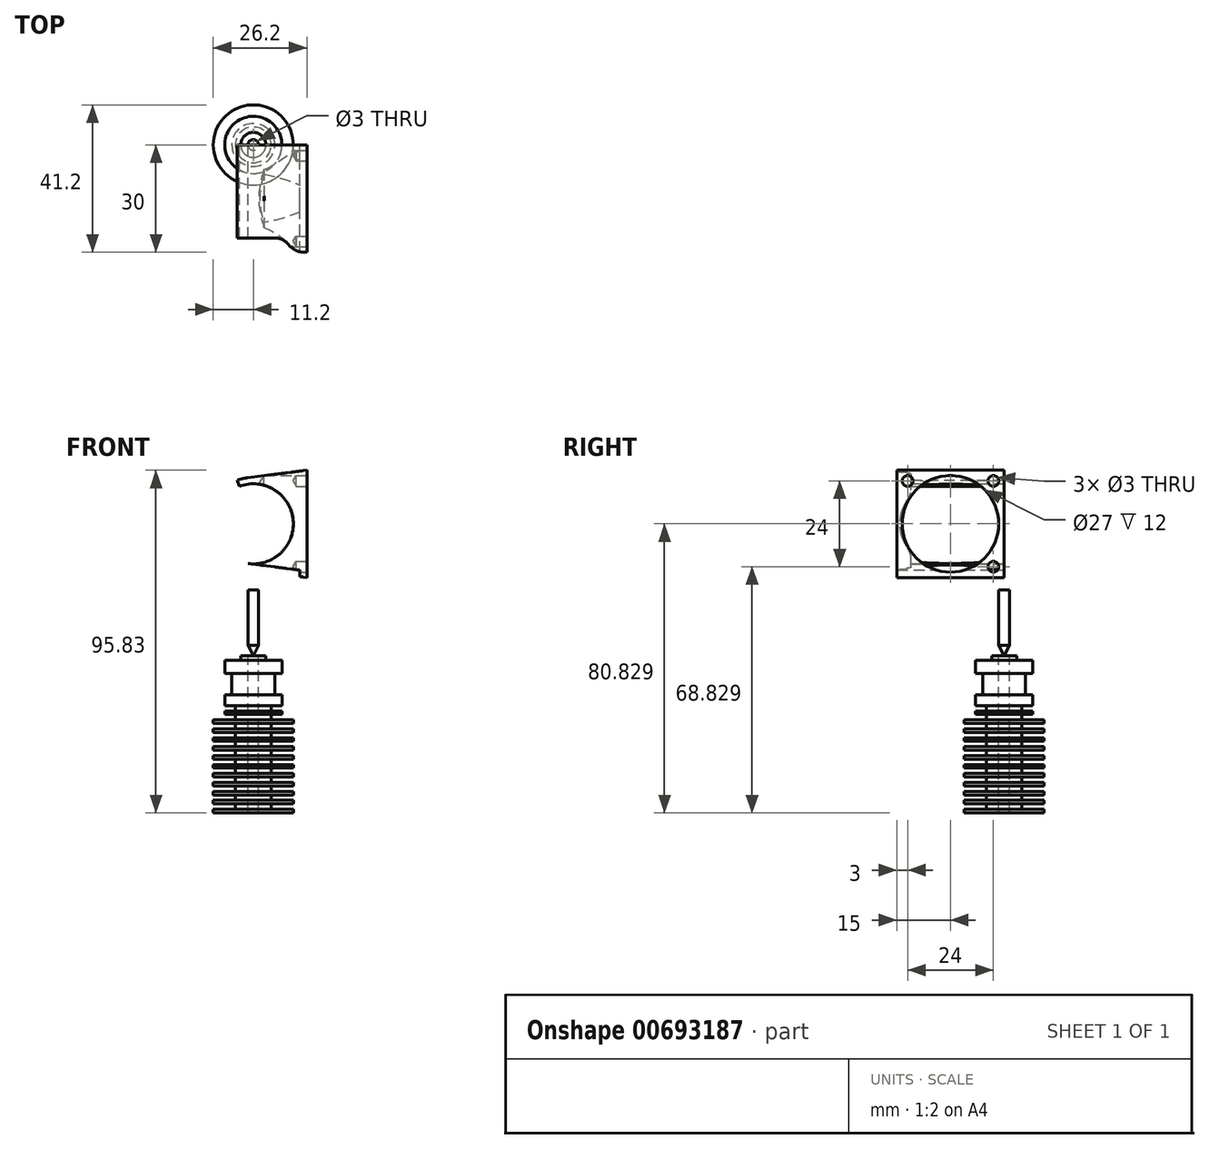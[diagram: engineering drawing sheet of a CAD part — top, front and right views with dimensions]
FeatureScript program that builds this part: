
annotation { "Feature Type Name" : "Feature", "Feature Type Description" : "" }
export const myFeature = defineFeature(function(context is Context, id is Id, definition is map)
    precondition{}
    {
        {
            var Q0;
            Q0=qCreatedBy(makeId("Front.planeOp"),FACE);
            var sketch = newSketch(context, id + "F0", { "sketchPlane" : qUnion([Q0])});
            skLineSegment(sketch, "E0.bottom", {"start": v(-3.5, 0) * mm, "end": v(3.5, 0) * mm});
            skLineSegment(sketch, "E0.top", {"start": v(-3.5, -1.2) * mm, "end": v(3.5, -1.2) * mm});
            skLineSegment(sketch, "E0.left", {"start": v(-3.5, 0) * mm, "end": v(-3.5, -1.2) * mm});
            skLineSegment(sketch, "E0.right", {"start": v(3.5, 0) * mm, "end": v(3.5, -1.2) * mm});
            skPoint(sketch, "E1", {"position": v(0, 0) * mm});
            skLineSegment(sketch, "E2", {"start": v(0, 5.65) * mm, "end": v(0, -51.62) * mm});
            skLineSegment(sketch, "E3.bottom", {"start": v(-8, -1.2) * mm, "end": v(8, -1.2) * mm});
            skLineSegment(sketch, "E3.top", {"start": v(-8, -4.9) * mm, "end": v(8, -4.9) * mm});
            skLineSegment(sketch, "E3.left", {"start": v(-8, -1.2) * mm, "end": v(-8, -4.9) * mm});
            skLineSegment(sketch, "E3.right", {"start": v(8, -1.2) * mm, "end": v(8, -4.9) * mm});
            skLineSegment(sketch, "E4.bottom", {"start": v(-8, -10.9) * mm, "end": v(8, -10.9) * mm});
            skLineSegment(sketch, "E4.top", {"start": v(-8, -13.9) * mm, "end": v(8, -13.9) * mm});
            skLineSegment(sketch, "E4.left", {"start": v(-8, -10.9) * mm, "end": v(-8, -13.9) * mm});
            skLineSegment(sketch, "E4.right", {"start": v(8, -10.9) * mm, "end": v(8, -13.9) * mm});
            skLineSegment(sketch, "E5.bottom", {"start": v(-6, -4.9) * mm, "end": v(6, -4.9) * mm});
            skLineSegment(sketch, "E5.top", {"start": v(-6, -10.9) * mm, "end": v(6, -10.9) * mm});
            skLineSegment(sketch, "E5.left", {"start": v(-6, -4.9) * mm, "end": v(-6, -10.9) * mm});
            skLineSegment(sketch, "E5.right", {"start": v(6, -4.9) * mm, "end": v(6, -10.9) * mm});
            skLineSegment(sketch, "E6.bottom", {"start": v(-11.2, -17.9) * mm, "end": v(11.2, -17.9) * mm});
            skLineSegment(sketch, "E6.top", {"start": v(-11.2, -18.9) * mm, "end": v(11.2, -18.9) * mm});
            skLineSegment(sketch, "E6.left", {"start": v(-11.2, -17.9) * mm, "end": v(-11.2, -18.9) * mm});
            skLineSegment(sketch, "E6.right", {"start": v(11.2, -17.9) * mm, "end": v(11.2, -18.9) * mm});
            skLineSegment(sketch, "E7.bottom", {"start": v(-8, -15.4) * mm, "end": v(8, -15.4) * mm});
            skLineSegment(sketch, "E7.top", {"start": v(-8, -16.4) * mm, "end": v(8, -16.4) * mm});
            skLineSegment(sketch, "E7.left", {"start": v(-8, -15.4) * mm, "end": v(-8, -16.4) * mm});
            skLineSegment(sketch, "E7.right", {"start": v(8, -15.4) * mm, "end": v(8, -16.4) * mm});
            skLineSegment(sketch, "E8.bottom", {"start": v(-5, -16.4) * mm, "end": v(5, -16.4) * mm});
            skLineSegment(sketch, "E8.top", {"start": v(-5, -43.9) * mm, "end": v(5, -43.9) * mm});
            skLineSegment(sketch, "E8.left", {"start": v(-5, -16.4) * mm, "end": v(-5, -43.9) * mm});
            skLineSegment(sketch, "E8.right", {"start": v(5, -16.4) * mm, "end": v(5, -43.9) * mm});
            skLineSegment(sketch, "E9.bottom", {"start": v(-5, -13.9) * mm, "end": v(5, -13.9) * mm});
            skLineSegment(sketch, "E9.top", {"start": v(-5, -15.4) * mm, "end": v(5, -15.4) * mm});
            skLineSegment(sketch, "E9.left", {"start": v(-5, -13.9) * mm, "end": v(-5, -15.4) * mm});
            skLineSegment(sketch, "E9.right", {"start": v(5, -13.9) * mm, "end": v(5, -15.4) * mm});
            skLineSegment(sketch, "E10", {"start": v(-23.04, -43.9) * mm, "end": v(22.42, -43.9) * mm, "construction": true});
            skLineSegment(sketch, "E11.bottom", {"start": v(-11.2, -42.9) * mm, "end": v(11.2, -42.9) * mm});
            skLineSegment(sketch, "E11.top", {"start": v(-11.2, -43.9) * mm, "end": v(11.2, -43.9) * mm});
            skLineSegment(sketch, "E11.left", {"start": v(-11.2, -42.9) * mm, "end": v(-11.2, -43.9) * mm});
            skLineSegment(sketch, "E11.right", {"start": v(11.2, -42.9) * mm, "end": v(11.2, -43.9) * mm});
            skLineSegment(sketch, "E12.bottom", {"start": v(-11.2, -40.4) * mm, "end": v(11.2, -40.4) * mm});
            skLineSegment(sketch, "E12.top", {"start": v(-11.2, -41.4) * mm, "end": v(11.2, -41.4) * mm});
            skLineSegment(sketch, "E12.left", {"start": v(-11.2, -40.4) * mm, "end": v(-11.2, -41.4) * mm});
            skLineSegment(sketch, "E12.right", {"start": v(11.2, -40.4) * mm, "end": v(11.2, -41.4) * mm});
            skLineSegment(sketch, "E13.bottom", {"start": v(-11.2, -37.9) * mm, "end": v(11.2, -37.9) * mm});
            skLineSegment(sketch, "E13.top", {"start": v(-11.2, -38.9) * mm, "end": v(11.2, -38.9) * mm});
            skLineSegment(sketch, "E13.left", {"start": v(-11.2, -37.9) * mm, "end": v(-11.2, -38.9) * mm});
            skLineSegment(sketch, "E13.right", {"start": v(11.2, -37.9) * mm, "end": v(11.2, -38.9) * mm});
            skLineSegment(sketch, "E14.bottom", {"start": v(-11.2, -35.4) * mm, "end": v(11.2, -35.4) * mm});
            skLineSegment(sketch, "E14.top", {"start": v(-11.2, -36.4) * mm, "end": v(11.2, -36.4) * mm});
            skLineSegment(sketch, "E14.left", {"start": v(-11.2, -35.4) * mm, "end": v(-11.2, -36.4) * mm});
            skLineSegment(sketch, "E14.right", {"start": v(11.2, -35.4) * mm, "end": v(11.2, -36.4) * mm});
            skLineSegment(sketch, "E15.bottom", {"start": v(-11.2, -32.9) * mm, "end": v(11.2, -32.9) * mm});
            skLineSegment(sketch, "E15.top", {"start": v(-11.2, -33.9) * mm, "end": v(11.2, -33.9) * mm});
            skLineSegment(sketch, "E15.left", {"start": v(-11.2, -32.9) * mm, "end": v(-11.2, -33.9) * mm});
            skLineSegment(sketch, "E15.right", {"start": v(11.2, -32.9) * mm, "end": v(11.2, -33.9) * mm});
            skLineSegment(sketch, "E16.bottom", {"start": v(-11.2, -30.4) * mm, "end": v(11.2, -30.4) * mm});
            skLineSegment(sketch, "E16.top", {"start": v(-11.2, -31.4) * mm, "end": v(11.2, -31.4) * mm});
            skLineSegment(sketch, "E16.left", {"start": v(-11.2, -30.4) * mm, "end": v(-11.2, -31.4) * mm});
            skLineSegment(sketch, "E16.right", {"start": v(11.2, -30.4) * mm, "end": v(11.2, -31.4) * mm});
            skLineSegment(sketch, "E17.bottom", {"start": v(-11.2, -27.9) * mm, "end": v(11.2, -27.9) * mm});
            skLineSegment(sketch, "E17.top", {"start": v(-11.2, -28.9) * mm, "end": v(11.2, -28.9) * mm});
            skLineSegment(sketch, "E17.left", {"start": v(-11.2, -27.9) * mm, "end": v(-11.2, -28.9) * mm});
            skLineSegment(sketch, "E17.right", {"start": v(11.2, -27.9) * mm, "end": v(11.2, -28.9) * mm});
            skLineSegment(sketch, "E18.bottom", {"start": v(-11.2, -25.4) * mm, "end": v(11.2, -25.4) * mm});
            skLineSegment(sketch, "E18.top", {"start": v(-11.2, -26.4) * mm, "end": v(11.2, -26.4) * mm});
            skLineSegment(sketch, "E18.left", {"start": v(-11.2, -25.4) * mm, "end": v(-11.2, -26.4) * mm});
            skLineSegment(sketch, "E18.right", {"start": v(11.2, -25.4) * mm, "end": v(11.2, -26.4) * mm});
            skLineSegment(sketch, "E19.bottom", {"start": v(-11.2, -22.9) * mm, "end": v(11.2, -22.9) * mm});
            skLineSegment(sketch, "E19.top", {"start": v(-11.2, -23.9) * mm, "end": v(11.2, -23.9) * mm});
            skLineSegment(sketch, "E19.left", {"start": v(-11.2, -22.9) * mm, "end": v(-11.2, -23.9) * mm});
            skLineSegment(sketch, "E19.right", {"start": v(11.2, -22.9) * mm, "end": v(11.2, -23.9) * mm});
            skLineSegment(sketch, "E20.bottom", {"start": v(-11.2, -20.4) * mm, "end": v(11.2, -20.4) * mm});
            skLineSegment(sketch, "E20.top", {"start": v(-11.2, -21.4) * mm, "end": v(11.2, -21.4) * mm});
            skLineSegment(sketch, "E20.left", {"start": v(-11.2, -20.4) * mm, "end": v(-11.2, -21.4) * mm});
            skLineSegment(sketch, "E20.right", {"start": v(11.2, -20.4) * mm, "end": v(11.2, -21.4) * mm});
            skLineSegment(sketch, "E21.bottom", {"start": v(29.22, -43.9) * mm, "end": v(59.22, -43.9) * mm});
            skLineSegment(sketch, "E21.top", {"start": v(29.22, -13.9) * mm, "end": v(59.22, -13.9) * mm});
            skLineSegment(sketch, "E21.left", {"start": v(29.22, -43.9) * mm, "end": v(29.22, -13.9) * mm});
            skLineSegment(sketch, "E21.right", {"start": v(59.22, -43.9) * mm, "end": v(59.22, -13.9) * mm});
            skLineSegment(sketch, "E22", {"start": v(87.52, -43.9) * mm, "end": v(112.52, -43.9) * mm});
            skLineSegment(sketch, "E23", {"start": v(112.52, -43.9) * mm, "end": v(112.52, -13.9) * mm});
            skLineSegment(sketch, "E24", {"start": v(112.52, -13.9) * mm, "end": v(102.52, -13.9) * mm});
            skLineSegment(sketch, "E25", {"start": v(102.52, -13.9) * mm, "end": v(102.52, -17.9) * mm});
            skLineSegment(sketch, "E26", {"start": v(102.52, -17.9) * mm, "end": v(87.52, -17.9) * mm});
            skLineSegment(sketch, "E27", {"start": v(87.52, -17.9) * mm, "end": v(87.52, -43.9) * mm});
            skCircle(sketch, "E28", {"center": v(0, 36.93) * mm, "radius": 11.2 * mm, "construction": true});
            skCircle(sketch, "E29", {"center": v(0, 36.93) * mm, "radius": 13 * mm, "construction": true});
            skLineSegment(sketch, "E30.right", {"start": v(25, 21.93) * mm, "end": v(25, 51.93) * mm});
            skLineSegment(sketch, "E31.right", {"start": v(15, 21.93) * mm, "end": v(15, 51.93) * mm});
            skLineSegment(sketch, "E32", {"start": v(15, 51.93) * mm, "end": v(-1.63, 49.83) * mm});
            skLineSegment(sketch, "E33", {"start": v(15, 21.93) * mm, "end": v(-1.63, 24.03) * mm});
            skLineSegment(sketch, "E34", {"start": v(15, 21.93) * mm, "end": v(25, 21.93) * mm});
            skLineSegment(sketch, "E35", {"start": v(15, 51.93) * mm, "end": v(25, 51.93) * mm});
            skLineSegment(sketch, "E36", {"start": v(0, 36.93) * mm, "end": v(-4.45, 49.15) * mm});
            skArc(sketch, "E37", {"start": v(-1.63, 49.83) * mm, "mid": v(-3.06, 49.56) * mm, "end": v(-4.45, 49.15) * mm});
            skPoint(sketch, "E38", {"position": v(15, 50.13) * mm});
            skPoint(sketch, "E39", {"position": v(15, 23.73) * mm});
            skLineSegment(sketch, "E40", {"start": v(15, 23.73) * mm, "end": v(-1.41, 25.82) * mm});
            skLineSegment(sketch, "E41", {"start": v(15, 50.13) * mm, "end": v(-1.41, 48.04) * mm});
            skLineSegment(sketch, "E42", {"start": v(0, 36.93) * mm, "end": v(-4.45, 24.71) * mm});
            skArc(sketch, "E43", {"start": v(-3.83, 47.45) * mm, "mid": v(11.2, 36.93) * mm, "end": v(-3.83, 26.4) * mm});
            skArc(sketch, "E44", {"start": v(-1.63, 24.03) * mm, "mid": v(-3.06, 24.3) * mm, "end": v(-4.45, 24.71) * mm});
            skLineSegment(sketch, "E45", {"start": v(0, 36.93) * mm, "end": v(33.8, 36.93) * mm, "construction": true});
            skLineSegment(sketch, "E46", {"start": v(13, 51.68) * mm, "end": v(13, 22.18) * mm});
            skSolve(sketch);
        }
        {
            var Q0;
            {var subQ0=sQuery(id+"F0.wireOp",EDGE,"E3.left");Q0=makeQuery(id+"F0.imprint","IMPRINT",FACE,{"disambiguationData":[TD([[makeQuery(id+"F0.imprint","IMPRINT",EDGE,{"derivedFrom":subQ0}),1.0]])]});}
            var Q1;
            {var subQ0=sQuery(id+"F0.wireOp",EDGE,"E0.left");Q1=makeQuery(id+"F0.imprint","IMPRINT",FACE,{"disambiguationData":[TD([[makeQuery(id+"F0.imprint","IMPRINT",EDGE,{"derivedFrom":subQ0}),1.0]])]});}
            var Q2;
            {var subQ5=sQuery(id+"F0.wireOp",EDGE,"E5.left");Q2=makeQuery(id+"F0.imprint","IMPRINT",FACE,{"disambiguationData":[TD([[makeQuery(id+"F0.imprint","IMPRINT",EDGE,{"derivedFrom":subQ5}),1.0]])]});}
            var Q3;
            {var subQ0=sQuery(id+"F0.wireOp",EDGE,"E4.left");Q3=makeQuery(id+"F0.imprint","IMPRINT",FACE,{"disambiguationData":[TD([[makeQuery(id+"F0.imprint","IMPRINT",EDGE,{"derivedFrom":subQ0}),1.0]])]});}
            var Q4;
            {var subQ5=sQuery(id+"F0.wireOp",EDGE,"E9.left");Q4=makeQuery(id+"F0.imprint","IMPRINT",FACE,{"disambiguationData":[TD([[makeQuery(id+"F0.imprint","IMPRINT",EDGE,{"derivedFrom":subQ5}),1.0]])]});}
            var Q5;
            {var subQ0=sQuery(id+"F0.wireOp",EDGE,"E7.left");Q5=makeQuery(id+"F0.imprint","IMPRINT",FACE,{"disambiguationData":[TD([[makeQuery(id+"F0.imprint","IMPRINT",EDGE,{"derivedFrom":subQ0}),1.0]])]});}
            var Q6;
            {var subQ0=sQuery(id+"F0.wireOp",EDGE,"E8.bottom");var subQ1=sQuery(id+"F0.wireOp",EDGE,"E2");var subQ2=makeQuery(id+"F0.imprint","INTERSECT",VERTEX,{"derivedFrom":[subQ1,subQ0]});Q6=makeQuery(id+"F0.imprint","IMPRINT",FACE,{"disambiguationData":[TD([[makeQuery(id+"F0.imprint","IMPRINT",EDGE,{"disambiguationData":[TD([[subQ2,-1.0]])],"derivedFrom":subQ1}),-1.0]])]});}
            var Q7;
            {var subQ0=sQuery(id+"F0.wireOp",EDGE,"E6.bottom");var subQ1=sQuery(id+"F0.wireOp",EDGE,"E2");var subQ2=makeQuery(id+"F0.imprint","INTERSECT",VERTEX,{"derivedFrom":[subQ1,subQ0]});Q7=makeQuery(id+"F0.imprint","IMPRINT",FACE,{"disambiguationData":[TD([[makeQuery(id+"F0.imprint","IMPRINT",EDGE,{"disambiguationData":[TD([[subQ2,-1.0]])],"derivedFrom":subQ1}),-1.0]])]});}
            var Q8;
            {var subQ0=sQuery(id+"F0.wireOp",EDGE,"E6.top");var subQ1=sQuery(id+"F0.wireOp",EDGE,"E2");var subQ2=makeQuery(id+"F0.imprint","INTERSECT",VERTEX,{"derivedFrom":[subQ1,subQ0]});Q8=makeQuery(id+"F0.imprint","IMPRINT",FACE,{"disambiguationData":[TD([[makeQuery(id+"F0.imprint","IMPRINT",EDGE,{"disambiguationData":[TD([[subQ2,-1.0]])],"derivedFrom":subQ1}),-1.0]])]});}
            var Q9;
            {var subQ0=sQuery(id+"F0.wireOp",EDGE,"E20.bottom");var subQ1=sQuery(id+"F0.wireOp",EDGE,"E2");var subQ2=makeQuery(id+"F0.imprint","INTERSECT",VERTEX,{"derivedFrom":[subQ1,subQ0]});Q9=makeQuery(id+"F0.imprint","IMPRINT",FACE,{"disambiguationData":[TD([[makeQuery(id+"F0.imprint","IMPRINT",EDGE,{"disambiguationData":[TD([[subQ2,-1.0]])],"derivedFrom":subQ1}),-1.0]])]});}
            var Q10;
            {var subQ0=sQuery(id+"F0.wireOp",EDGE,"E19.bottom");var subQ1=sQuery(id+"F0.wireOp",EDGE,"E2");var subQ2=makeQuery(id+"F0.imprint","INTERSECT",VERTEX,{"derivedFrom":[subQ1,subQ0]});Q10=makeQuery(id+"F0.imprint","IMPRINT",FACE,{"disambiguationData":[TD([[makeQuery(id+"F0.imprint","IMPRINT",EDGE,{"disambiguationData":[TD([[subQ2,-1.0]])],"derivedFrom":subQ1}),-1.0]])]});}
            var Q11;
            {var subQ5=sQuery(id+"F0.wireOp",EDGE,"E20.left");Q11=makeQuery(id+"F0.imprint","IMPRINT",FACE,{"disambiguationData":[TD([[makeQuery(id+"F0.imprint","IMPRINT",EDGE,{"derivedFrom":subQ5}),1.0]])]});}
            var Q12;
            {var subQ5=sQuery(id+"F0.wireOp",EDGE,"E19.left");Q12=makeQuery(id+"F0.imprint","IMPRINT",FACE,{"disambiguationData":[TD([[makeQuery(id+"F0.imprint","IMPRINT",EDGE,{"derivedFrom":subQ5}),1.0]])]});}
            var Q13;
            {var subQ5=sQuery(id+"F0.wireOp",EDGE,"E18.left");Q13=makeQuery(id+"F0.imprint","IMPRINT",FACE,{"disambiguationData":[TD([[makeQuery(id+"F0.imprint","IMPRINT",EDGE,{"derivedFrom":subQ5}),1.0]])]});}
            var Q14;
            {var subQ5=sQuery(id+"F0.wireOp",EDGE,"E17.left");Q14=makeQuery(id+"F0.imprint","IMPRINT",FACE,{"disambiguationData":[TD([[makeQuery(id+"F0.imprint","IMPRINT",EDGE,{"derivedFrom":subQ5}),1.0]])]});}
            var Q15;
            {var subQ5=sQuery(id+"F0.wireOp",EDGE,"E15.left");Q15=makeQuery(id+"F0.imprint","IMPRINT",FACE,{"disambiguationData":[TD([[makeQuery(id+"F0.imprint","IMPRINT",EDGE,{"derivedFrom":subQ5}),1.0]])]});}
            var Q16;
            {var subQ5=sQuery(id+"F0.wireOp",EDGE,"E16.left");Q16=makeQuery(id+"F0.imprint","IMPRINT",FACE,{"disambiguationData":[TD([[makeQuery(id+"F0.imprint","IMPRINT",EDGE,{"derivedFrom":subQ5}),1.0]])]});}
            var Q17;
            {var subQ5=sQuery(id+"F0.wireOp",EDGE,"E13.left");Q17=makeQuery(id+"F0.imprint","IMPRINT",FACE,{"disambiguationData":[TD([[makeQuery(id+"F0.imprint","IMPRINT",EDGE,{"derivedFrom":subQ5}),1.0]])]});}
            var Q18;
            {var subQ5=sQuery(id+"F0.wireOp",EDGE,"E12.left");Q18=makeQuery(id+"F0.imprint","IMPRINT",FACE,{"disambiguationData":[TD([[makeQuery(id+"F0.imprint","IMPRINT",EDGE,{"derivedFrom":subQ5}),1.0]])]});}
            var Q19;
            {var subQ5=sQuery(id+"F0.wireOp",EDGE,"E14.left");Q19=makeQuery(id+"F0.imprint","IMPRINT",FACE,{"disambiguationData":[TD([[makeQuery(id+"F0.imprint","IMPRINT",EDGE,{"derivedFrom":subQ5}),1.0]])]});}
            var Q20;
            {var subQ5=sQuery(id+"F0.wireOp",EDGE,"E11.left");Q20=makeQuery(id+"F0.imprint","IMPRINT",FACE,{"disambiguationData":[TD([[makeQuery(id+"F0.imprint","IMPRINT",EDGE,{"derivedFrom":subQ5}),1.0]])]});}
            var Q21;
            {var subQ0=sQuery(id+"F0.wireOp",EDGE,"E18.bottom");var subQ1=sQuery(id+"F0.wireOp",EDGE,"E2");var subQ2=makeQuery(id+"F0.imprint","INTERSECT",VERTEX,{"derivedFrom":[subQ1,subQ0]});Q21=makeQuery(id+"F0.imprint","IMPRINT",FACE,{"disambiguationData":[TD([[makeQuery(id+"F0.imprint","IMPRINT",EDGE,{"disambiguationData":[TD([[subQ2,-1.0]])],"derivedFrom":subQ1}),-1.0]])]});}
            var Q22;
            {var subQ0=sQuery(id+"F0.wireOp",EDGE,"E6.left");Q22=makeQuery(id+"F0.imprint","IMPRINT",FACE,{"disambiguationData":[TD([[makeQuery(id+"F0.imprint","IMPRINT",EDGE,{"derivedFrom":subQ0}),1.0]])]});}
            var Q23;
            {var subQ0=sQuery(id+"F0.wireOp",EDGE,"E18.top");var subQ1=sQuery(id+"F0.wireOp",EDGE,"E2");var subQ2=makeQuery(id+"F0.imprint","INTERSECT",VERTEX,{"derivedFrom":[subQ1,subQ0]});Q23=makeQuery(id+"F0.imprint","IMPRINT",FACE,{"disambiguationData":[TD([[makeQuery(id+"F0.imprint","IMPRINT",EDGE,{"disambiguationData":[TD([[subQ2,-1.0]])],"derivedFrom":subQ1}),-1.0]])]});}
            var Q24;
            {var subQ0=sQuery(id+"F0.wireOp",EDGE,"E19.top");var subQ1=sQuery(id+"F0.wireOp",EDGE,"E2");var subQ2=makeQuery(id+"F0.imprint","INTERSECT",VERTEX,{"derivedFrom":[subQ1,subQ0]});Q24=makeQuery(id+"F0.imprint","IMPRINT",FACE,{"disambiguationData":[TD([[makeQuery(id+"F0.imprint","IMPRINT",EDGE,{"disambiguationData":[TD([[subQ2,-1.0]])],"derivedFrom":subQ1}),-1.0]])]});}
            var Q25;
            {var subQ0=sQuery(id+"F0.wireOp",EDGE,"E20.top");var subQ1=sQuery(id+"F0.wireOp",EDGE,"E2");var subQ2=makeQuery(id+"F0.imprint","INTERSECT",VERTEX,{"derivedFrom":[subQ1,subQ0]});Q25=makeQuery(id+"F0.imprint","IMPRINT",FACE,{"disambiguationData":[TD([[makeQuery(id+"F0.imprint","IMPRINT",EDGE,{"disambiguationData":[TD([[subQ2,-1.0]])],"derivedFrom":subQ1}),-1.0]])]});}
            var Q26;
            {var subQ0=sQuery(id+"F0.wireOp",EDGE,"E12.top");var subQ1=sQuery(id+"F0.wireOp",EDGE,"E2");var subQ2=makeQuery(id+"F0.imprint","INTERSECT",VERTEX,{"derivedFrom":[subQ1,subQ0]});Q26=makeQuery(id+"F0.imprint","IMPRINT",FACE,{"disambiguationData":[TD([[makeQuery(id+"F0.imprint","IMPRINT",EDGE,{"disambiguationData":[TD([[subQ2,-1.0]])],"derivedFrom":subQ1}),-1.0]])]});}
            var Q27;
            {var subQ0=sQuery(id+"F0.wireOp",EDGE,"E13.top");var subQ1=sQuery(id+"F0.wireOp",EDGE,"E2");var subQ2=makeQuery(id+"F0.imprint","INTERSECT",VERTEX,{"derivedFrom":[subQ1,subQ0]});Q27=makeQuery(id+"F0.imprint","IMPRINT",FACE,{"disambiguationData":[TD([[makeQuery(id+"F0.imprint","IMPRINT",EDGE,{"disambiguationData":[TD([[subQ2,-1.0]])],"derivedFrom":subQ1}),-1.0]])]});}
            var Q28;
            {var subQ0=sQuery(id+"F0.wireOp",EDGE,"E17.top");var subQ1=sQuery(id+"F0.wireOp",EDGE,"E2");var subQ2=makeQuery(id+"F0.imprint","INTERSECT",VERTEX,{"derivedFrom":[subQ1,subQ0]});Q28=makeQuery(id+"F0.imprint","IMPRINT",FACE,{"disambiguationData":[TD([[makeQuery(id+"F0.imprint","IMPRINT",EDGE,{"disambiguationData":[TD([[subQ2,-1.0]])],"derivedFrom":subQ1}),-1.0]])]});}
            var Q29;
            {var subQ0=sQuery(id+"F0.wireOp",EDGE,"E16.top");var subQ1=sQuery(id+"F0.wireOp",EDGE,"E2");var subQ2=makeQuery(id+"F0.imprint","INTERSECT",VERTEX,{"derivedFrom":[subQ1,subQ0]});Q29=makeQuery(id+"F0.imprint","IMPRINT",FACE,{"disambiguationData":[TD([[makeQuery(id+"F0.imprint","IMPRINT",EDGE,{"disambiguationData":[TD([[subQ2,-1.0]])],"derivedFrom":subQ1}),-1.0]])]});}
            var Q30;
            {var subQ0=sQuery(id+"F0.wireOp",EDGE,"E14.top");var subQ1=sQuery(id+"F0.wireOp",EDGE,"E2");var subQ2=makeQuery(id+"F0.imprint","INTERSECT",VERTEX,{"derivedFrom":[subQ1,subQ0]});Q30=makeQuery(id+"F0.imprint","IMPRINT",FACE,{"disambiguationData":[TD([[makeQuery(id+"F0.imprint","IMPRINT",EDGE,{"disambiguationData":[TD([[subQ2,-1.0]])],"derivedFrom":subQ1}),-1.0]])]});}
            var Q31;
            {var subQ0=sQuery(id+"F0.wireOp",EDGE,"E17.bottom");var subQ1=sQuery(id+"F0.wireOp",EDGE,"E2");var subQ2=makeQuery(id+"F0.imprint","INTERSECT",VERTEX,{"derivedFrom":[subQ1,subQ0]});Q31=makeQuery(id+"F0.imprint","IMPRINT",FACE,{"disambiguationData":[TD([[makeQuery(id+"F0.imprint","IMPRINT",EDGE,{"disambiguationData":[TD([[subQ2,-1.0]])],"derivedFrom":subQ1}),-1.0]])]});}
            var Q32;
            {var subQ0=sQuery(id+"F0.wireOp",EDGE,"E16.bottom");var subQ1=sQuery(id+"F0.wireOp",EDGE,"E2");var subQ2=makeQuery(id+"F0.imprint","INTERSECT",VERTEX,{"derivedFrom":[subQ1,subQ0]});Q32=makeQuery(id+"F0.imprint","IMPRINT",FACE,{"disambiguationData":[TD([[makeQuery(id+"F0.imprint","IMPRINT",EDGE,{"disambiguationData":[TD([[subQ2,-1.0]])],"derivedFrom":subQ1}),-1.0]])]});}
            var Q33;
            {var subQ0=sQuery(id+"F0.wireOp",EDGE,"E15.bottom");var subQ1=sQuery(id+"F0.wireOp",EDGE,"E2");var subQ2=makeQuery(id+"F0.imprint","INTERSECT",VERTEX,{"derivedFrom":[subQ1,subQ0]});Q33=makeQuery(id+"F0.imprint","IMPRINT",FACE,{"disambiguationData":[TD([[makeQuery(id+"F0.imprint","IMPRINT",EDGE,{"disambiguationData":[TD([[subQ2,-1.0]])],"derivedFrom":subQ1}),-1.0]])]});}
            var Q34;
            {var subQ0=sQuery(id+"F0.wireOp",EDGE,"E12.bottom");var subQ1=sQuery(id+"F0.wireOp",EDGE,"E2");var subQ2=makeQuery(id+"F0.imprint","INTERSECT",VERTEX,{"derivedFrom":[subQ1,subQ0]});Q34=makeQuery(id+"F0.imprint","IMPRINT",FACE,{"disambiguationData":[TD([[makeQuery(id+"F0.imprint","IMPRINT",EDGE,{"disambiguationData":[TD([[subQ2,-1.0]])],"derivedFrom":subQ1}),-1.0]])]});}
            var Q35;
            {var subQ0=sQuery(id+"F0.wireOp",EDGE,"E13.bottom");var subQ1=sQuery(id+"F0.wireOp",EDGE,"E2");var subQ2=makeQuery(id+"F0.imprint","INTERSECT",VERTEX,{"derivedFrom":[subQ1,subQ0]});Q35=makeQuery(id+"F0.imprint","IMPRINT",FACE,{"disambiguationData":[TD([[makeQuery(id+"F0.imprint","IMPRINT",EDGE,{"disambiguationData":[TD([[subQ2,-1.0]])],"derivedFrom":subQ1}),-1.0]])]});}
            var Q36;
            {var subQ0=sQuery(id+"F0.wireOp",EDGE,"E15.top");var subQ1=sQuery(id+"F0.wireOp",EDGE,"E2");var subQ2=makeQuery(id+"F0.imprint","INTERSECT",VERTEX,{"derivedFrom":[subQ1,subQ0]});Q36=makeQuery(id+"F0.imprint","IMPRINT",FACE,{"disambiguationData":[TD([[makeQuery(id+"F0.imprint","IMPRINT",EDGE,{"disambiguationData":[TD([[subQ2,-1.0]])],"derivedFrom":subQ1}),-1.0]])]});}
            var Q37;
            {var subQ0=sQuery(id+"F0.wireOp",EDGE,"E14.bottom");var subQ1=sQuery(id+"F0.wireOp",EDGE,"E2");var subQ2=makeQuery(id+"F0.imprint","INTERSECT",VERTEX,{"derivedFrom":[subQ1,subQ0]});Q37=makeQuery(id+"F0.imprint","IMPRINT",FACE,{"disambiguationData":[TD([[makeQuery(id+"F0.imprint","IMPRINT",EDGE,{"disambiguationData":[TD([[subQ2,-1.0]])],"derivedFrom":subQ1}),-1.0]])]});}
            var Q38;
            {var subQ0=sQuery(id+"F0.wireOp",EDGE,"E11.top");var subQ1=sQuery(id+"F0.wireOp",EDGE,"E2");var subQ2=makeQuery(id+"F0.imprint","INTERSECT",VERTEX,{"derivedFrom":[subQ1,subQ0]});Q38=makeQuery(id+"F0.imprint","IMPRINT",FACE,{"disambiguationData":[TD([[makeQuery(id+"F0.imprint","IMPRINT",EDGE,{"disambiguationData":[TD([[subQ2,1.0]])],"derivedFrom":subQ1}),-1.0]])]});}
            var Q39;
            Q39=sQuery(id+"F0.wireOp",EDGE,"E2");
            revolve(context, id + "F1", {"entities" : qUnion([Q0, Q1, Q2, Q3, Q4, Q5, Q6, Q7, Q8, Q9, Q10, Q11, Q12, Q13, Q14, Q15, Q16, Q17, Q18, Q19, Q20, Q21, Q22, Q23, Q24, Q25, Q26, Q27, Q28, Q29, Q30, Q31, Q32, Q33, Q34, Q35, Q36, Q37, Q38]), "axis" : qUnion([Q39]), "revolveType" : RevolveType.FULL});
        }
        {
            var Q0;
            Q0=makeQuery(id+"F1.opRevolve","SWEPT_FACE",FACE,{"disambiguationData":[OSD([sQuery(id+"F0.wireOp",EDGE,"E0.bottom")])]});
            var sketch = newSketch(context, id + "F2", { "sketchPlane" : qUnion([Q0])});
            skPoint(sketch, "E47", {"position": v(0, 0) * mm});
            skSolve(sketch);
        }
        {
            var Q0;
            Q0=sQuery(id+"F2.wireOp",VERTEX,"E47");
            var Q1;
            Q1=makeQuery(id+"F1.opRevolve","SWEPT_BODY",BODY,{"disambiguationData":[OSD([sQuery(id+"F0.wireOp",EDGE,"E0.bottom"),sQuery(id+"F0.wireOp",EDGE,"E0.left"),sQuery(id+"F0.wireOp",EDGE,"E2"),sQuery(id+"F0.wireOp",EDGE,"E3.bottom"),sQuery(id+"F0.wireOp",EDGE,"E3.top"),sQuery(id+"F0.wireOp",EDGE,"E3.left"),sQuery(id+"F0.wireOp",EDGE,"E4.bottom"),sQuery(id+"F0.wireOp",EDGE,"E4.top"),sQuery(id+"F0.wireOp",EDGE,"E4.left"),sQuery(id+"F0.wireOp",EDGE,"E5.left"),sQuery(id+"F0.wireOp",EDGE,"E6.bottom"),sQuery(id+"F0.wireOp",EDGE,"E6.top"),sQuery(id+"F0.wireOp",EDGE,"E6.left"),sQuery(id+"F0.wireOp",EDGE,"E7.bottom"),sQuery(id+"F0.wireOp",EDGE,"E7.top"),sQuery(id+"F0.wireOp",EDGE,"E7.left"),sQuery(id+"F0.wireOp",EDGE,"E8.left"),sQuery(id+"F0.wireOp",EDGE,"E9.left"),sQuery(id+"F0.wireOp",EDGE,"E11.bottom"),sQuery(id+"F0.wireOp",EDGE,"E11.top"),sQuery(id+"F0.wireOp",EDGE,"E11.left"),sQuery(id+"F0.wireOp",EDGE,"E12.bottom"),sQuery(id+"F0.wireOp",EDGE,"E12.top"),sQuery(id+"F0.wireOp",EDGE,"E12.left"),sQuery(id+"F0.wireOp",EDGE,"E13.bottom"),sQuery(id+"F0.wireOp",EDGE,"E13.top"),sQuery(id+"F0.wireOp",EDGE,"E13.left"),sQuery(id+"F0.wireOp",EDGE,"E14.bottom"),sQuery(id+"F0.wireOp",EDGE,"E14.top"),sQuery(id+"F0.wireOp",EDGE,"E14.left"),sQuery(id+"F0.wireOp",EDGE,"E15.bottom"),sQuery(id+"F0.wireOp",EDGE,"E15.top"),sQuery(id+"F0.wireOp",EDGE,"E15.left"),sQuery(id+"F0.wireOp",EDGE,"E16.bottom"),sQuery(id+"F0.wireOp",EDGE,"E16.top"),sQuery(id+"F0.wireOp",EDGE,"E16.left"),sQuery(id+"F0.wireOp",EDGE,"E17.bottom"),sQuery(id+"F0.wireOp",EDGE,"E17.top"),sQuery(id+"F0.wireOp",EDGE,"E17.left"),sQuery(id+"F0.wireOp",EDGE,"E18.bottom"),sQuery(id+"F0.wireOp",EDGE,"E18.top"),sQuery(id+"F0.wireOp",EDGE,"E18.left"),sQuery(id+"F0.wireOp",EDGE,"E19.bottom"),sQuery(id+"F0.wireOp",EDGE,"E19.top"),sQuery(id+"F0.wireOp",EDGE,"E19.left"),sQuery(id+"F0.wireOp",EDGE,"E20.bottom"),sQuery(id+"F0.wireOp",EDGE,"E20.top"),sQuery(id+"F0.wireOp",EDGE,"E20.left")])]});
            hole(context, id + "F3", {"style" : HoleStyle.SIMPLE, "endStyle" : HoleEndStyle.THROUGH, "holeDiameter" : 3 * mm, "majorDiameter" : 5 * mm, "isTappedThrough" : true, "tappedDepth" : 12 * mm, "tapClearance" : 3, "locations" : qUnion([Q0]), "scope" : qUnion([Q1])});
        }
        {
            var Q0;
            {var subQ0=sQuery(id+"F0.wireOp",EDGE,"E40");Q0=makeQuery(id+"F0.imprint","IMPRINT",FACE,{"disambiguationData":[TD([[makeQuery(id+"F0.imprint","IMPRINT",EDGE,{"derivedFrom":subQ0}),-1.0]])]});}
            var Q1;
            {var subQ4=sQuery(id+"F0.wireOp",EDGE,"E32");Q1=makeQuery(id+"F0.imprint","IMPRINT",FACE,{"disambiguationData":[TD([[makeQuery(id+"F0.imprint","IMPRINT",EDGE,{"derivedFrom":subQ4}),1.0]])]});}
            var Q2;
            {var subQ4=sQuery(id+"F0.wireOp",EDGE,"E33");Q2=makeQuery(id+"F0.imprint","IMPRINT",FACE,{"disambiguationData":[TD([[makeQuery(id+"F0.imprint","IMPRINT",EDGE,{"derivedFrom":subQ4}),-1.0]])]});}
            var Q3;
            {var subQ0=sQuery(id+"F0.wireOp",EDGE,"E37");Q3=makeQuery(id+"F0.imprint","IMPRINT",FACE,{"disambiguationData":[TD([[makeQuery(id+"F0.imprint","IMPRINT",EDGE,{"derivedFrom":subQ0}),1.0]])]});}
            var Q4;
            {var subQ5=sQuery(id+"F0.wireOp",EDGE,"E44");Q4=makeQuery(id+"F0.imprint","IMPRINT",FACE,{"disambiguationData":[TD([[makeQuery(id+"F0.imprint","IMPRINT",EDGE,{"derivedFrom":subQ5}),-1.0]])]});}
            extrude(context, id + "F4", {"entities" : qUnion([Q0, Q1, Q2, Q3, Q4]), "depth" : 26 * mm, "offsetDistance" : 25 * mm});
        }
        {
            var Q0;
            {var subQ5=sQuery(id+"F0.wireOp",EDGE,"E46");Q0=makeQuery(id+"F0.imprint","IMPRINT",FACE,{"disambiguationData":[TD([[makeQuery(id+"F0.imprint","IMPRINT",EDGE,{"derivedFrom":subQ5}),1.0]])]});}
            extrude(context, id + "F5", {"entities" : qUnion([Q0]), "operationType" : NewBodyOperationType.ADD, "depth" : 30 * mm, "offsetDistance" : 25 * mm});
        }
        {
            var Q0;
            Q0=makeQuery(id+"F5.boolean.opBoolean","INTERSECT",EDGE,{"derivedFrom":[makeQuery(id+"F4.opExtrude","CAP_FACE",FACE,{"disambiguationData":[OSD([sQuery(id+"F0.wireOp",EDGE,"E31.right"),sQuery(id+"F0.wireOp",EDGE,"E32"),sQuery(id+"F0.wireOp",EDGE,"E33"),sQuery(id+"F0.wireOp",EDGE,"E36"),sQuery(id+"F0.wireOp",EDGE,"E37"),sQuery(id+"F0.wireOp",EDGE,"E42"),sQuery(id+"F0.wireOp",EDGE,"E43"),sQuery(id+"F0.wireOp",EDGE,"E44")])],"isStart":false}),makeQuery(id+"F5.opExtrude","SWEPT_FACE",FACE,{"disambiguationData":[OSD([sQuery(id+"F0.wireOp",EDGE,"E46")])]})]});
            chamfer(context, id + "F6", {"entities" : qUnion([Q0]), "width" : 5 * mm, "tangentPropagation" : true});
        }
        {
            var Q0;
            {var subQ0=makeQuery(id+"F4.opExtrude","CAP_FACE",FACE,{"disambiguationData":[OSD([sQuery(id+"F0.wireOp",EDGE,"E31.right"),sQuery(id+"F0.wireOp",EDGE,"E32"),sQuery(id+"F0.wireOp",EDGE,"E33"),sQuery(id+"F0.wireOp",EDGE,"E36"),sQuery(id+"F0.wireOp",EDGE,"E37"),sQuery(id+"F0.wireOp",EDGE,"E42"),sQuery(id+"F0.wireOp",EDGE,"E43"),sQuery(id+"F0.wireOp",EDGE,"E44")])],"isStart":false});Q0=makeQuery(id+"F6.opChamfer","BLEND_EDGE",EDGE,{"disambiguationData":[OD(0.0)],"blendedFrom":[makeQuery(id+"F5.boolean.opBoolean","INTERSECT",EDGE,{"derivedFrom":[subQ0,makeQuery(id+"F5.opExtrude","SWEPT_FACE",FACE,{"disambiguationData":[OSD([sQuery(id+"F0.wireOp",EDGE,"E46")])]})]}),subQ0],"blendedInto":[subQ0]});}
            var Q1;
            {var subQ0=makeQuery(id+"F4.opExtrude","CAP_FACE",FACE,{"disambiguationData":[OSD([sQuery(id+"F0.wireOp",EDGE,"E31.right"),sQuery(id+"F0.wireOp",EDGE,"E32"),sQuery(id+"F0.wireOp",EDGE,"E33"),sQuery(id+"F0.wireOp",EDGE,"E36"),sQuery(id+"F0.wireOp",EDGE,"E37"),sQuery(id+"F0.wireOp",EDGE,"E42"),sQuery(id+"F0.wireOp",EDGE,"E43"),sQuery(id+"F0.wireOp",EDGE,"E44")])],"isStart":false});Q1=makeQuery(id+"F6.opChamfer","BLEND_EDGE",EDGE,{"disambiguationData":[OD(1.0)],"blendedFrom":[makeQuery(id+"F5.boolean.opBoolean","INTERSECT",EDGE,{"derivedFrom":[subQ0,makeQuery(id+"F5.opExtrude","SWEPT_FACE",FACE,{"disambiguationData":[OSD([sQuery(id+"F0.wireOp",EDGE,"E46")])]})]}),subQ0],"blendedInto":[subQ0]});}
            var Q2;
            {var subQ0=sQuery(id+"F0.wireOp",EDGE,"E46");var subQ1=sQuery(id+"F0.wireOp",EDGE,"E33");var subQ2=sQuery(id+"F0.wireOp",EDGE,"E32");var subQ3=sQuery(id+"F0.wireOp",EDGE,"E31.right");Q2=makeQuery(id+"F6.opChamfer","BLEND_EDGE",EDGE,{"blendedFrom":[makeQuery(id+"F5.boolean.opBoolean","INTERSECT",EDGE,{"derivedFrom":[makeQuery(id+"F4.opExtrude","CAP_FACE",FACE,{"disambiguationData":[OSD([subQ3,subQ2,subQ1,sQuery(id+"F0.wireOp",EDGE,"E36"),sQuery(id+"F0.wireOp",EDGE,"E37"),sQuery(id+"F0.wireOp",EDGE,"E42"),sQuery(id+"F0.wireOp",EDGE,"E43"),sQuery(id+"F0.wireOp",EDGE,"E44")])],"isStart":false}),makeQuery(id+"F5.opExtrude","SWEPT_FACE",FACE,{"disambiguationData":[OSD([subQ0])]})]}),makeQuery(id+"F5.opExtrude","CAP_FACE",FACE,{"disambiguationData":[OSD([subQ3,subQ2,subQ1,subQ0])],"isStart":false})],"blendedInto":[makeQuery(id+"F5.opExtrude","CAP_FACE",FACE,{"disambiguationData":[OSD([subQ3,subQ2,subQ1,subQ0])],"isStart":false})]});}
            fillet(context, id + "F7", {"entities" : qUnion([Q0, Q1, Q2]), "radius" : 5 * mm, "tangentPropagation" : true, "allowEdgeOverflow" : false});
        }
        {
            var Q0;
            {var subQ0=sQuery(id+"F0.wireOp",EDGE,"E31.right");Q0=makeQuery(id+"F5.boolean.opBoolean","MERGE",FACE,{"derivedFrom":[makeQuery(id+"F4.opExtrude","SWEPT_FACE",FACE,{"disambiguationData":[OSD([subQ0])]}),makeQuery(id+"F5.opExtrude","SWEPT_FACE",FACE,{"disambiguationData":[OSD([subQ0])]})]});}
            var sketch = newSketch(context, id + "F8", { "sketchPlane" : qUnion([Q0])});
            skLineSegment(sketch, "E48", {"start": v(-30, 51.93) * mm, "end": v(0, 21.93) * mm, "construction": true});
            skPoint(sketch, "E49", {"position": v(-15, 36.93) * mm});
            skLineSegment(sketch, "E50.bottom", {"start": v(-30, 51.93) * mm, "end": v(0, 51.93) * mm, "construction": true});
            skLineSegment(sketch, "E50.top", {"start": v(-30, 21.93) * mm, "end": v(0, 21.93) * mm, "construction": true});
            skLineSegment(sketch, "E50.left", {"start": v(-30, 51.93) * mm, "end": v(-30, 21.93) * mm, "construction": true});
            skLineSegment(sketch, "E50.right", {"start": v(0, 51.93) * mm, "end": v(0, 21.93) * mm, "construction": true});
            skPoint(sketch, "E51", {"position": v(-27, 48.93) * mm});
            skPoint(sketch, "E52", {"position": v(-3, 24.93) * mm});
            skPoint(sketch, "E53", {"position": v(-3, 48.93) * mm});
            skSolve(sketch);
        }
        {
            var Q0;
            Q0=qCreatedBy(makeId("Front.planeOp"),FACE);
            var sketch = newSketch(context, id + "F9", { "sketchPlane" : qUnion([Q0])});
            skLineSegment(sketch, "E54", {"start": v(0, 0) * mm, "end": v(0, 18.4) * mm});
            skLineSegment(sketch, "E55", {"start": v(-1.5, 0) * mm, "end": v(-1.5, 18.4) * mm});
            skLineSegment(sketch, "E56", {"start": v(1.5, 0) * mm, "end": v(1.5, 18.4) * mm});
            skLineSegment(sketch, "E57", {"start": v(-1.5, 18.4) * mm, "end": v(1.5, 18.4) * mm});
            skLineSegment(sketch, "E58", {"start": v(-1.5, 3) * mm, "end": v(1.5, 3) * mm});
            skLineSegment(sketch, "E59", {"start": v(-1.5, 3) * mm, "end": v(0, 0) * mm});
            skLineSegment(sketch, "E60", {"start": v(1.5, 3) * mm, "end": v(0, 0) * mm});
            skSolve(sketch);
        }
        {
            var Q0;
            {var subQ0=sQuery(id+"F9.wireOp",EDGE,"E57");var subQ1=sQuery(id+"F9.wireOp",EDGE,"E54");var subQ2=makeQuery(id+"F9.imprint","INTERSECT",VERTEX,{"derivedFrom":[subQ1,subQ0]});Q0=makeQuery(id+"F9.imprint","IMPRINT",FACE,{"disambiguationData":[TD([[makeQuery(id+"F9.imprint","IMPRINT",EDGE,{"disambiguationData":[TD([[subQ2,1.0]])],"derivedFrom":subQ1}),1.0]])]});}
            var Q1;
            {var subQ0=sQuery(id+"F9.wireOp",EDGE,"E59");Q1=makeQuery(id+"F9.imprint","IMPRINT",FACE,{"disambiguationData":[TD([[makeQuery(id+"F9.imprint","IMPRINT",EDGE,{"derivedFrom":subQ0}),1.0]])]});}
            var Q2;
            Q2=sQuery(id+"F9.wireOp",EDGE,"E54");
            revolve(context, id + "F10", {"entities" : qUnion([Q0, Q1]), "axis" : qUnion([Q2]), "revolveType" : RevolveType.FULL});
        }
        {
            var Q0;
            Q0=sQuery(id+"F8.wireOp",VERTEX,"E51");
            var Q1;
            Q1=sQuery(id+"F8.wireOp",VERTEX,"E52");
            var Q2;
            Q2=sQuery(id+"F8.wireOp",VERTEX,"E53");
            var Q3;
            Q3=makeQuery(id+"F4.opExtrude","SWEPT_BODY",BODY,{"disambiguationData":[OSD([sQuery(id+"F0.wireOp",EDGE,"E31.right"),sQuery(id+"F0.wireOp",EDGE,"E32"),sQuery(id+"F0.wireOp",EDGE,"E33"),sQuery(id+"F0.wireOp",EDGE,"E36"),sQuery(id+"F0.wireOp",EDGE,"E37"),sQuery(id+"F0.wireOp",EDGE,"E42"),sQuery(id+"F0.wireOp",EDGE,"E43"),sQuery(id+"F0.wireOp",EDGE,"E44")])]});
            hole(context, id + "F11", {"style" : HoleStyle.SIMPLE, "endStyle" : HoleEndStyle.BLIND, "holeDiameter" : 3 * mm, "majorDiameter" : 5 * mm, "holeDepth" : 3 * mm, "isTappedThrough" : true, "tappedDepth" : 12 * mm, "tapClearance" : 3, "locations" : qUnion([Q0, Q1, Q2]), "scope" : qUnion([Q3])});
        }
        {
            var Q0;
            Q0=sQuery(id+"F8.wireOp",VERTEX,"E49");
            var Q1;
            Q1=makeQuery(id+"F4.opExtrude","SWEPT_BODY",BODY,{"disambiguationData":[OSD([sQuery(id+"F0.wireOp",EDGE,"E31.right"),sQuery(id+"F0.wireOp",EDGE,"E32"),sQuery(id+"F0.wireOp",EDGE,"E33"),sQuery(id+"F0.wireOp",EDGE,"E36"),sQuery(id+"F0.wireOp",EDGE,"E37"),sQuery(id+"F0.wireOp",EDGE,"E42"),sQuery(id+"F0.wireOp",EDGE,"E43"),sQuery(id+"F0.wireOp",EDGE,"E44")])]});
            hole(context, id + "F12", {"style" : HoleStyle.SIMPLE, "endStyle" : HoleEndStyle.BLIND, "holeDiameter" : 27 * mm, "majorDiameter" : 5 * mm, "holeDepth" : 12 * mm, "isTappedThrough" : true, "tappedDepth" : 12 * mm, "tapClearance" : 3, "locations" : qUnion([Q0]), "scope" : qUnion([Q1])});
        }
    });
